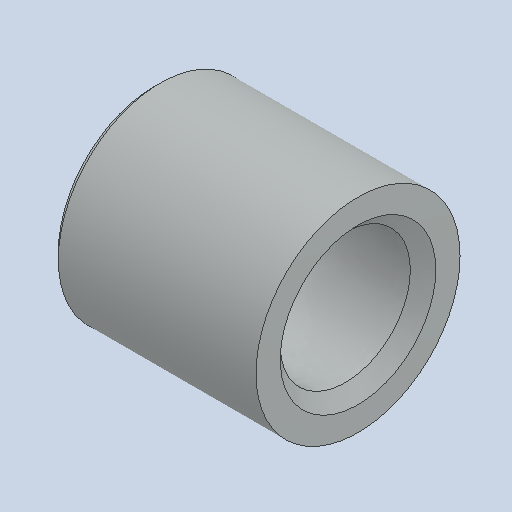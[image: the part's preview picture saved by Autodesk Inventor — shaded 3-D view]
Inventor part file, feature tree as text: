
AUTODESK INVENTOR PART (.ipt)
format: ipt  version: 2024.1 (Build 281209000, 209)  size: 115,712 bytes
history: native  units: in
note: dims shown in document units (in); Inventor stores cm internally (conversion verified against a paired STEP export)
features: chamfer x1
ambient origin geometry x8: Origin, YZ Plane, XZ Plane, XY Plane, X Axis, Y Axis, Z Axis, Center Point
bodies: Solid1 (feature_tree)
feature tree (1):
  chamfer  "Chamfer2"  [1 undecoded]
note: 1 required parameter value undecoded (feature->parameter linkage not recoverable at this tier; creation-order binding heuristic only, values carry confidence <= 0.55)
